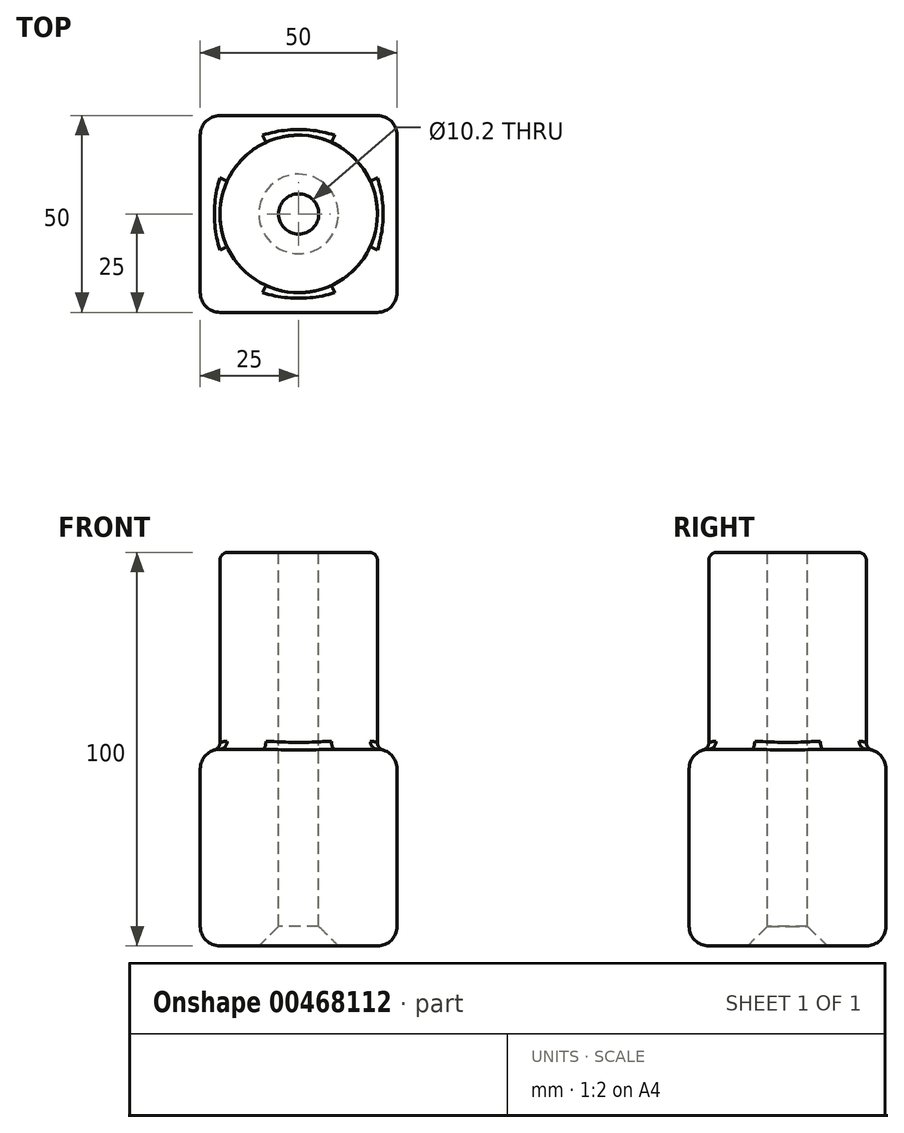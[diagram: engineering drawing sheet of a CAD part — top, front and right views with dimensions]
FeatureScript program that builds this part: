
annotation { "Feature Type Name" : "Feature", "Feature Type Description" : "" }
export const myFeature = defineFeature(function(context is Context, id is Id, definition is map)
    precondition{}
    {
        {
            var Q0;
            Q0=qCreatedBy(makeId("Front.planeOp"),FACE);
            var sketch = newSketch(context, id + "F0", { "sketchPlane" : qUnion([Q0])});
            skLineSegment(sketch, "E0.bottom", {"start": v(-25, 25) * mm, "end": v(25, 25) * mm});
            skLineSegment(sketch, "E0.top", {"start": v(-25, -25) * mm, "end": v(25, -25) * mm});
            skLineSegment(sketch, "E0.left", {"start": v(-25, 25) * mm, "end": v(-25, -25) * mm});
            skLineSegment(sketch, "E0.right", {"start": v(25, 25) * mm, "end": v(25, -25) * mm});
            skPoint(sketch, "E0.middle", {"position": v(0, 0) * mm});
            skSolve(sketch);
        }
        {
            var Q0;
            Q0=makeQuery(id+"F0.imprint","IMPRINT",FACE,{"disambiguationData":[TD([[makeQuery(id+"F0.imprint","IMPRINT",EDGE,{"derivedFrom":sQuery(id+"F0.wireOp",EDGE,"E0.bottom")}),-1.0]])]});
            extrude(context, id + "F1", {"entities" : qUnion([Q0]), "endBound" : BoundingType.SYMMETRIC, "depth" : 50 * mm});
        }
        {
            var Q0;
            Q0=makeQuery(id+"F1.opExtrude","CAP_EDGE",EDGE,{"disambiguationData":[OSD([sQuery(id+"F0.wireOp",EDGE,"E0.right")])],"isStart":false});
            var Q1;
            Q1=makeQuery(id+"F1.opExtrude","SWEPT_FACE",FACE,{"disambiguationData":[OSD([sQuery(id+"F0.wireOp",EDGE,"E0.right")])]});
            var Q2;
            Q2=makeQuery(id+"F1.opExtrude","CAP_FACE",FACE,{"disambiguationData":[OSD([sQuery(id+"F0.wireOp",EDGE,"E0.bottom"),sQuery(id+"F0.wireOp",EDGE,"E0.top"),sQuery(id+"F0.wireOp",EDGE,"E0.left"),sQuery(id+"F0.wireOp",EDGE,"E0.right")])],"isStart":false});
            var Q3;
            Q3=makeQuery(id+"F1.opExtrude","SWEPT_FACE",FACE,{"disambiguationData":[OSD([sQuery(id+"F0.wireOp",EDGE,"E0.bottom")])]});
            var Q4;
            Q4=makeQuery(id+"F1.opExtrude","SWEPT_FACE",FACE,{"disambiguationData":[OSD([sQuery(id+"F0.wireOp",EDGE,"E0.left")])]});
            var Q5;
            Q5=makeQuery(id+"F1.opExtrude","CAP_FACE",FACE,{"disambiguationData":[OSD([sQuery(id+"F0.wireOp",EDGE,"E0.bottom"),sQuery(id+"F0.wireOp",EDGE,"E0.top"),sQuery(id+"F0.wireOp",EDGE,"E0.left"),sQuery(id+"F0.wireOp",EDGE,"E0.right")])],"isStart":true});
            fillet(context, id + "F2", {"entities" : qUnion([Q0, Q1, Q2, Q3, Q4, Q5]), "radius" : 5 * mm, "tangentPropagation" : true, "allowEdgeOverflow" : false});
        }
        {
            var Q0;
            Q0=makeQuery(id+"F1.opExtrude","SWEPT_FACE",FACE,{"disambiguationData":[OSD([sQuery(id+"F0.wireOp",EDGE,"E0.bottom")])]});
            var sketch = newSketch(context, id + "F3", { "sketchPlane" : qUnion([Q0])});
            skCircle(sketch, "E1", {"center": v(0, 0) * mm, "radius": 20 * mm});
            skSolve(sketch);
        }
        {
            var Q0;
            {var subQ0=sQuery(id+"F3.wireOp",EDGE,"E1");var subQ1=sQuery(id+"F0.wireOp",EDGE,"E0.bottom");var subQ2=makeQuery(id+"F1.opExtrude","SWEPT_FACE",FACE,{"disambiguationData":[OSD([subQ1])]});var subQ3=makeQuery(id+"F3.imprint","INTERSECT",VERTEX,{"derivedFrom":[makeQuery(id+"F2.opFillet","BLEND_EDGE",EDGE,{"blendedFrom":[makeQuery(id+"F1.opExtrude","CAP_EDGE",EDGE,{"disambiguationData":[OSD([subQ1])],"isStart":true}),subQ2],"blendedInto":[subQ2]}),subQ0]});Q0=makeQuery(id+"F3.imprint","IMPRINT",FACE,{"disambiguationData":[TD([[makeQuery(id+"F3.imprint","IMPRINT",EDGE,{"disambiguationData":[TD([[subQ3,1.0]])],"derivedFrom":subQ0}),1.0]])]});}
            extrude(context, id + "F4", {"entities" : qUnion([Q0]), "operationType" : NewBodyOperationType.ADD, "depth" : 50 * mm});
        }
        {
            var Q0;
            Q0=makeQuery(id+"F4.opExtrude","CAP_FACE",FACE,{"disambiguationData":[OSD([sQuery(id+"F3.wireOp",EDGE,"E1")])],"isStart":false});
            fillet(context, id + "F5", {"entities" : qUnion([Q0]), "radius" : 2 * mm, "tangentPropagation" : true, "allowEdgeOverflow" : false});
        }
        {
            var Q0;
            {var subQ0=sQuery(id+"F0.wireOp",EDGE,"E0.bottom");var subQ1=sQuery(id+"F0.wireOp",EDGE,"E0.left");var subQ2=sQuery(id+"F3.wireOp",EDGE,"E1");Q0=makeQuery(id+"F4.boolean.opBoolean","SPLIT",EDGE,{"disambiguationData":[TD([makeQuery(id+"F1.opExtrude","SWEPT_FACE",FACE,{"disambiguationData":[OSD([subQ0])]}),makeQuery(id+"F2.opFillet","BLEND_FACE",FACE,{"disambiguationData":[OSD([subQ0,subQ1]),TDD([makeQuery(id+"F1.opExtrude","SWEPT_EDGE",EDGE,{"disambiguationData":[OSD([subQ0,subQ1])]})])]}),makeQuery(id+"F2.opFillet","BLEND_FACE",FACE,{"disambiguationData":[OSD([subQ0]),TDD([makeQuery(id+"F1.opExtrude","CAP_EDGE",EDGE,{"disambiguationData":[OSD([subQ0])],"isStart":false})])]}),makeQuery(id+"F4.opExtrude","SWEPT_FACE",FACE,{"disambiguationData":[OSD([subQ2])]})])],"derivedFrom":makeQuery(id+"F4.opExtrude","CAP_EDGE",EDGE,{"disambiguationData":[OSD([subQ2])],"isStart":true})});}
            fillet(context, id + "F6", {"entities" : qUnion([Q0]), "radius" : 2 * mm, "tangentPropagation" : true, "allowEdgeOverflow" : false});
        }
        {
            var Q0;
            Q0=makeQuery(id+"F4.opExtrude","CAP_FACE",FACE,{"disambiguationData":[OSD([sQuery(id+"F3.wireOp",EDGE,"E1")])],"isStart":false});
            var sketch = newSketch(context, id + "F7", { "sketchPlane" : qUnion([Q0])});
            skCircle(sketch, "E2", {"center": v(0, 0) * mm, "radius": 5.1 * mm});
            skSolve(sketch);
        }
        {
            var Q0;
            Q0=makeQuery(id+"F7.imprint","IMPRINT",FACE,{"disambiguationData":[TD([[makeQuery(id+"F7.imprint","IMPRINT",EDGE,{"derivedFrom":sQuery(id+"F7.wireOp",EDGE,"E2")}),1.0]])]});
            extrude(context, id + "F8", {"entities" : qUnion([Q0]), "operationType" : NewBodyOperationType.REMOVE, "endBound" : BoundingType.THROUGH_ALL, "oppositeDirection" : true, "depth" : 25 * mm});
        }
        {
            var Q0;
            Q0=makeQuery(id+"F8.boolean.opBoolean","INTERSECT",EDGE,{"derivedFrom":[makeQuery(id+"F1.opExtrude","SWEPT_FACE",FACE,{"disambiguationData":[OSD([sQuery(id+"F0.wireOp",EDGE,"E0.top")])]}),makeQuery(id+"F8.opExtrude","SWEPT_FACE",FACE,{"disambiguationData":[OSD([sQuery(id+"F7.wireOp",EDGE,"E2")])]})]});
            var Q1;
            Q1=makeQuery(id+"F8.boolean.opBoolean","COPY",EDGE,{"derivedFrom":makeQuery(id+"F8.opExtrude","CAP_EDGE",EDGE,{"disambiguationData":[OSD([sQuery(id+"F7.wireOp",EDGE,"E2")])],"isStart":true})});
            chamfer(context, id + "F9", {"entities" : qUnion([Q0, Q1]), "width" : 5 * mm, "tangentPropagation" : true});
        }
    });
